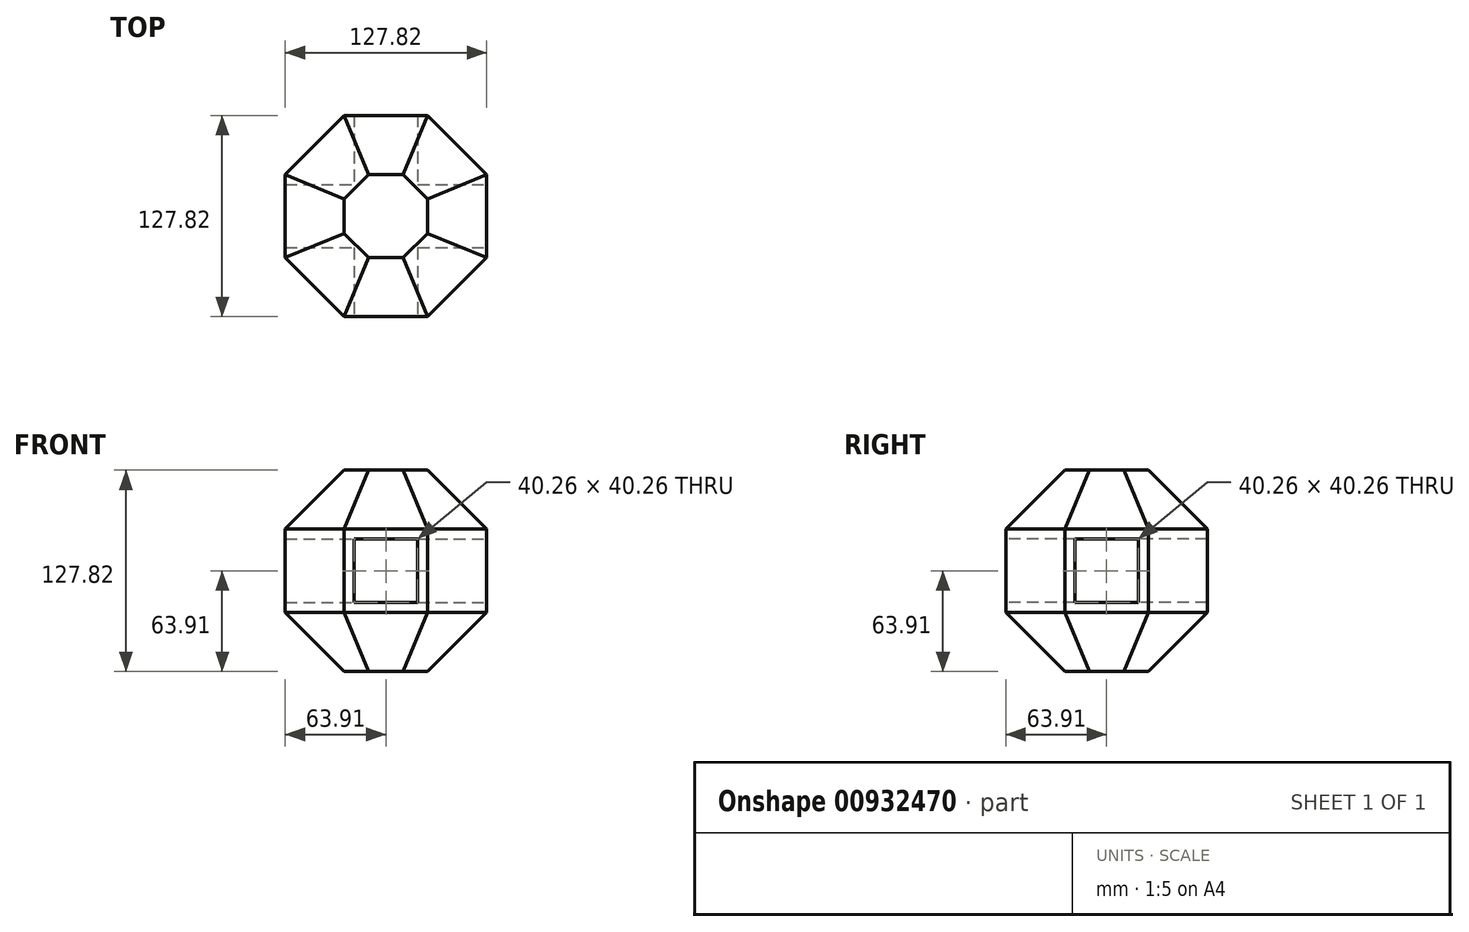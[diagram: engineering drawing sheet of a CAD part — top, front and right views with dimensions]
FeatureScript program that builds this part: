
annotation { "Feature Type Name" : "Feature", "Feature Type Description" : "" }
export const myFeature = defineFeature(function(context is Context, id is Id, definition is map)
    precondition{}
    {
        {
            var Q0;
            Q0=qCreatedBy(makeId("Top.planeOp"),FACE);
            var sketch = newSketch(context, id + "F0", { "sketchPlane" : qUnion([Q0])});
            skCircle(sketch, "E0.cCircle", {"center": v(0, 0) * mm, "radius": 63.5 * mm, "construction": true});
            skLineSegment(sketch, "E0.0", {"start": v(-63.5, -26.3) * mm, "end": v(-63.5, 26.3) * mm});
            skLineSegment(sketch, "E0.1", {"start": v(-63.5, 26.3) * mm, "end": v(-26.3, 63.5) * mm});
            skLineSegment(sketch, "E0.2", {"start": v(-26.3, 63.5) * mm, "end": v(26.3, 63.5) * mm});
            skLineSegment(sketch, "E0.3", {"start": v(26.3, 63.5) * mm, "end": v(63.5, 26.3) * mm});
            skLineSegment(sketch, "E0.4", {"start": v(63.5, 26.3) * mm, "end": v(63.5, -26.3) * mm});
            skLineSegment(sketch, "E0.5", {"start": v(63.5, -26.3) * mm, "end": v(26.3, -63.5) * mm});
            skLineSegment(sketch, "E0.6", {"start": v(26.3, -63.5) * mm, "end": v(-26.3, -63.5) * mm});
            skLineSegment(sketch, "E0.7", {"start": v(-26.3, -63.5) * mm, "end": v(-63.5, -26.3) * mm});
            skPoint(sketch, "E0.0.midPoint", {"position": v(-63.5, 0) * mm});
            skSolve(sketch);
        }
        {
            var Q0;
            Q0=qCreatedBy(makeId("Front.planeOp"),FACE);
            var sketch = newSketch(context, id + "F1", { "sketchPlane" : qUnion([Q0])});
            skCircle(sketch, "E1.cCircle", {"center": v(0, 0) * mm, "radius": 63.9 * mm, "construction": true});
            skLineSegment(sketch, "E1.2", {"start": v(0, -63.9) * mm, "end": v(-26.47, -63.9) * mm});
            skLineSegment(sketch, "E1.3", {"start": v(-26.47, -63.9) * mm, "end": v(-63.9, -26.47) * mm});
            skLineSegment(sketch, "E1.4", {"start": v(-63.9, -26.47) * mm, "end": v(-63.9, 26.47) * mm});
            skLineSegment(sketch, "E1.5", {"start": v(-63.9, 26.47) * mm, "end": v(-26.47, 63.9) * mm});
            skLineSegment(sketch, "E1.6", {"start": v(-26.47, 63.9) * mm, "end": v(0, 63.9) * mm});
            skPoint(sketch, "E1.0.midPoint", {"position": v(63.9, 0) * mm});
            skLineSegment(sketch, "E2", {"start": v(0, 63.9) * mm, "end": v(0, -63.9) * mm, "construction": true});
            skLineSegment(sketch, "E3", {"start": v(0, 63.9) * mm, "end": v(0, -63.9) * mm});
            skSolve(sketch);
        }
        {
            var Q0;
            Q0=makeQuery(id+"F1.imprint","IMPRINT",FACE,{"disambiguationData":[TD([[makeQuery(id+"F1.imprint","IMPRINT",EDGE,{"derivedFrom":sQuery(id+"F1.wireOp",EDGE,"E1.2")}),-1.0]])]});
            var Q1;
            Q1=sQuery(id+"F0.wireOp",EDGE,"E0.1");
            var Q2;
            Q2=sQuery(id+"F0.wireOp",EDGE,"E0.0");
            var Q3;
            Q3=sQuery(id+"F0.wireOp",EDGE,"E0.2");
            var Q4;
            Q4=sQuery(id+"F0.wireOp",EDGE,"E0.3");
            var Q5;
            Q5=sQuery(id+"F0.wireOp",EDGE,"E0.4");
            var Q6;
            Q6=sQuery(id+"F0.wireOp",EDGE,"E0.5");
            var Q7;
            Q7=sQuery(id+"F0.wireOp",EDGE,"E0.6");
            var Q8;
            Q8=sQuery(id+"F0.wireOp",EDGE,"E0.7");
            sweep(context, id + "F2", {"profiles" : qUnion([Q0]), "path" : qUnion([Q1, Q2, Q3, Q4, Q5, Q6, Q7, Q8])});
        }
        {
            var Q0;
            Q0=makeQuery(id+"F2.opSweep","SWEPT_FACE",FACE,{"disambiguationData":[OSD([sQuery(id+"F0.wireOp",EDGE,"E0.4"),sQuery(id+"F1.wireOp",EDGE,"E1.4")])]});
            var sketch = newSketch(context, id + "F3", { "sketchPlane" : qUnion([Q0])});
            skLineSegment(sketch, "E4.bottom", {"start": v(-20.13, 20.13) * mm, "end": v(20.13, 20.13) * mm});
            skLineSegment(sketch, "E4.top", {"start": v(-20.13, -20.13) * mm, "end": v(20.13, -20.13) * mm});
            skLineSegment(sketch, "E4.left", {"start": v(-20.13, 20.13) * mm, "end": v(-20.13, -20.13) * mm});
            skLineSegment(sketch, "E4.right", {"start": v(20.13, 20.13) * mm, "end": v(20.13, -20.13) * mm});
            skLineSegment(sketch, "E5", {"start": v(-20.13, 20.13) * mm, "end": v(-26.47, 26.47) * mm, "construction": true});
            skLineSegment(sketch, "E6", {"start": v(20.13, 20.13) * mm, "end": v(26.47, 26.47) * mm, "construction": true});
            skLineSegment(sketch, "E7", {"start": v(26.47, -26.47) * mm, "end": v(20.13, -20.13) * mm, "construction": true});
            skLineSegment(sketch, "E8", {"start": v(-20.13, -20.13) * mm, "end": v(-26.47, -26.47) * mm, "construction": true});
            skSolve(sketch);
        }
        {
            var Q0;
            Q0=makeQuery(id+"F3.imprint","IMPRINT",FACE,{"disambiguationData":[TD([[makeQuery(id+"F3.imprint","IMPRINT",EDGE,{"derivedFrom":sQuery(id+"F3.wireOp",EDGE,"E4.bottom")}),-1.0]])]});
            extrude(context, id + "F4", {"entities" : qUnion([Q0]), "operationType" : NewBodyOperationType.REMOVE, "endBound" : BoundingType.THROUGH_ALL, "oppositeDirection" : true, "depth" : 25.4 * mm, "offsetDistance" : 25.4 * mm});
        }
        {
            var Q0;
            Q0=makeQuery(id+"F2.opSweep","SWEPT_FACE",FACE,{"disambiguationData":[OSD([sQuery(id+"F0.wireOp",EDGE,"E0.6"),sQuery(id+"F1.wireOp",EDGE,"E1.4")])]});
            var sketch = newSketch(context, id + "F5", { "sketchPlane" : qUnion([Q0])});
            skLineSegment(sketch, "E9.bottom", {"start": v(-20.13, 20.13) * mm, "end": v(20.13, 20.13) * mm});
            skLineSegment(sketch, "E9.top", {"start": v(-20.13, -20.13) * mm, "end": v(20.13, -20.13) * mm});
            skLineSegment(sketch, "E9.left", {"start": v(-20.13, 20.13) * mm, "end": v(-20.13, -20.13) * mm});
            skLineSegment(sketch, "E9.right", {"start": v(20.13, 20.13) * mm, "end": v(20.13, -20.13) * mm});
            skLineSegment(sketch, "E10", {"start": v(-20.13, 20.13) * mm, "end": v(-26.47, 26.47) * mm, "construction": true});
            skLineSegment(sketch, "E11", {"start": v(20.13, 20.13) * mm, "end": v(26.47, 26.47) * mm, "construction": true});
            skLineSegment(sketch, "E12", {"start": v(20.13, -20.13) * mm, "end": v(26.47, -26.47) * mm, "construction": true});
            skLineSegment(sketch, "E13", {"start": v(-20.13, -20.13) * mm, "end": v(-26.47, -26.47) * mm, "construction": true});
            skSolve(sketch);
        }
        {
            var Q0;
            Q0=makeQuery(id+"F5.imprint","IMPRINT",FACE,{"disambiguationData":[TD([[makeQuery(id+"F5.imprint","IMPRINT",EDGE,{"derivedFrom":sQuery(id+"F5.wireOp",EDGE,"E9.bottom")}),-1.0]])]});
            extrude(context, id + "F6", {"entities" : qUnion([Q0]), "operationType" : NewBodyOperationType.REMOVE, "endBound" : BoundingType.THROUGH_ALL, "oppositeDirection" : true, "depth" : 25.4 * mm, "offsetDistance" : 25.4 * mm});
        }
    });
